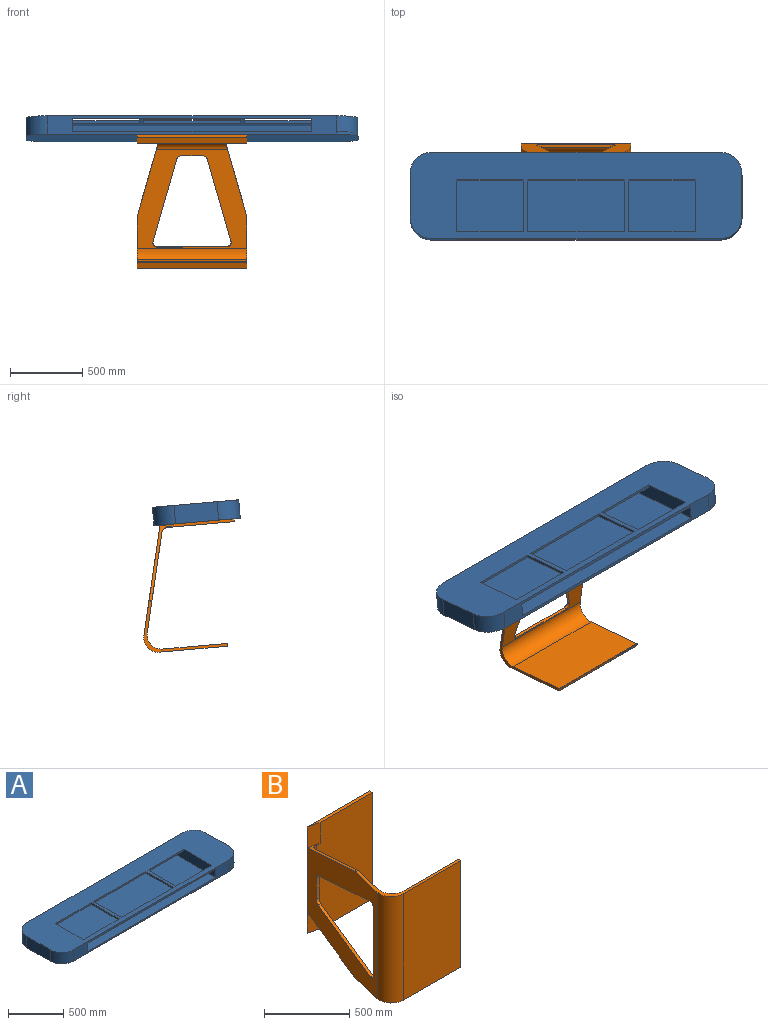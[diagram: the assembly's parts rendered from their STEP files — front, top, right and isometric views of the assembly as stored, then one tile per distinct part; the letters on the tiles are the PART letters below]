
ASSEMBLY  parts=2 mates=1
PART A: 28 faces, bbox 2300x600x128 mm
  f0: plane 1652x582mm, normal (0,0,1), area 961464mm2, adj f1,f6,f19,f27
  f1: plane 582x110mm, normal (-1,0,0), area 59988mm2, adj f0,f6,f13,f18,f21,f22,f27
  f2: plane 2000x128mm, normal (0,1,0), area 256000mm2, adj f3,f20,f21,f23,f26
  f3: cylinder r=150mm len=150mm, axis (0,0,-1), area 30159.3mm2, adj f2,f4,f21,f26
  f4: plane 300x128mm, normal (-1,0,0), area 38400mm2, adj f3,f5,f21,f26
  f5: cylinder r=150mm len=150mm, axis (0,0,-1), area 30159.3mm2, adj f4,f6,f21,f26
  f6: plane 2000x128mm, normal (0,-1,0), area 104016mm2, adj f0,f1,f5,f7,f19,f21,f22,f25
  f7: cylinder r=150mm len=150mm, axis (0,0,-1), area 25918.1mm2, adj f6,f8,f21,f25
  f8: plane 300x110mm, normal (1,0,0), area 33000mm2, adj f7,f20,f21,f24
  f9: plane 357x18mm, normal (-1,0,0), area 6426mm2, adj f10,f17,f21,f22
  f10: plane 668x18mm, normal (0,1,0), area 12024mm2, adj f9,f11,f21,f22
  f11: plane 357x18mm, normal (1,0,0), area 6426mm2, adj f10,f17,f21,f22
  f12: plane 358x18mm, normal (1,0,0), area 6444mm2, adj f13,f18,f21,f22
  f13: plane 462x18mm, normal (0,-1,0), area 8316mm2, adj f1,f12,f21,f22
  f14: plane 462x18mm, normal (0,-1,0), area 8316mm2, adj f15,f19,f21,f22
  f15: plane 358x18mm, normal (-1,0,0), area 6444mm2, adj f14,f16,f21,f22
  f16: plane 462x18mm, normal (0,1,0), area 8316mm2, adj f15,f19,f21,f22
  f17: plane 668x18mm, normal (0,-1,0), area 12024mm2, adj f9,f11,f21,f22
  f18: plane 462x18mm, normal (0,1,0), area 8316mm2, adj f1,f12,f21,f22
  f19: plane 582x110mm, normal (1,0,0), area 59988mm2, adj f0,f6,f14,f16,f21,f22,f27
  f20: cylinder r=150mm len=150mm, axis (0,0,-1), area 25918.1mm2, adj f2,f8,f21,f23
  f21: plane 2300x600mm, normal (0,0,1), area 791417.8mm2, adj f1,f2,f3,f4,f5,f6,f7,f8
  f22: plane 1652x582mm, normal (0,0,-1), area 392196mm2, adj f1,f6,f9,f10,f11,f12,f13,f14
  f23: cylinder r=150mm len=150mm, axis (0,0,1), area 4241.2mm2, adj f2,f20,f24,f26
  f24: plane 300x18mm, normal (1,0,0), area 5400mm2, adj f8,f23,f25,f26
  f25: cylinder r=150mm len=150mm, axis (0,0,1), area 4241.2mm2, adj f6,f7,f24,f26
  f26: plane 2300x600mm, normal (0,0,-1), area 1360685.8mm2, adj f2,f3,f4,f5,f6,f23,f24,f25
  f27: plane 1652x92mm, normal (0,-1,0), area 151984mm2, adj f0,f1,f19,f22
PART B: 31 faces, bbox 696.7x875.8x762 mm
  f0: plane 762x674.83mm, normal (0.97,-0.23,0), area 222758.4mm2, adj f2,f3,f10,f11,f17,f18,f19,f20
  f1: plane 762x752.78mm, normal (-0.97,0.23,0), area 268039.9mm2, adj f2,f3,f4,f14,f17,f18,f19,f20
  f2: plane 577.65x357.08mm, normal (0,0,1), area 18567mm2, adj f0,f1,f4,f5,f6,f7,f8,f9
  f3: plane 577.65x357.07mm, normal (0,0,-1), area 18566.9mm2, adj f0,f1,f4,f5,f6,f7,f8,f9
  f4: cylinder r=100mm len=762mm, axis (0,0,-1), area 137402.9mm2, adj f1,f2,f3,f5
  f5: plane 762x471.99mm, normal (0,-1,0), area 359655.6mm2, adj f2,f3,f4,f6
  f6: cylinder r=2mm len=762mm, axis (0,0,-1), area 2039.7mm2, adj f2,f3,f5,f7
  f7: plane 762x15.46mm, normal (0.97,-0.23,0), area 12107.8mm2, adj f2,f3,f6,f8
  f8: cylinder r=2mm len=762mm, axis (0,0,-1), area 2748.1mm2, adj f2,f3,f7,f9
  f9: plane 762x450.49mm, normal (0,1,0), area 343273.3mm2, adj f2,f3,f8,f10
  f10: cylinder r=100mm len=762mm, axis (0,0,-1), area 137402.9mm2, adj f0,f2,f3,f9
  f11: cylinder r=50mm len=493.16mm, axis (0,0,-1), area 31910.2mm2, adj f0,f12,f21,f24
  f12: plane 762x460.45mm, normal (0,-1,0), area 342170.1mm2, adj f11,f13,f15,f16,f21,f22,f23,f24
  f13: plane 762x20mm, normal (1,0,0), area 15240mm2, adj f12,f14,f15,f16
  f14: plane 762x515.82mm, normal (0,1,0), area 393054.2mm2, adj f1,f13,f15,f16,f22,f23
  f15: plane 515.82x20mm, normal (0,0,1), area 9471.3mm2, adj f12,f13,f14,f23
  f16: plane 515.82x20mm, normal (0,0,-1), area 9471.3mm2, adj f12,f13,f14,f22
  f17: plane 154.66x19.46mm, normal (-0.23,-0.97,0), area 3093.2mm2, adj f0,f1,f25,f28
  f18: plane 566.21x163.98mm, normal (-0.06,-0.27,0.96), area 11999.2mm2, adj f0,f1,f27,f28
  f19: plane 482.6x19.69mm, normal (0.23,0.97,0), area 9652mm2, adj f0,f1,f26,f27
  f20: plane 567.17x163.96mm, normal (-0.06,-0.27,-0.96), area 12018.1mm2, adj f0,f1,f25,f26
  f21: plane 515.36x205.39mm, normal (0.06,0.27,-0.96), area 11778.8mm2, adj f0,f1,f11,f12,f22,f30
  f22: plane 150.27x84.51mm, normal (-0.23,-0.97,0), area 13049.7mm2, adj f12,f14,f16,f21
  f23: plane 150x84.51mm, normal (-0.23,-0.97,0), area 13026.2mm2, adj f12,f14,f15,f24
  f24: plane 515.37x205.39mm, normal (0.06,0.27,0.96), area 11777.4mm2, adj f0,f1,f11,f12,f23,f29
  f25: cylinder r=30mm len=28.86mm, axis (0.97,-0.23,0), area 776.7mm2, adj f0,f1,f17,f20
  f26: cylinder r=30mm len=41.77mm, axis (0.97,-0.23,0), area 1109.5mm2, adj f0,f1,f19,f20
  f27: cylinder r=30mm len=41.78mm, axis (-0.97,0.23,0), area 1107.3mm2, adj f0,f1,f18,f19
  f28: cylinder r=30mm len=28.86mm, axis (-0.97,0.23,0), area 776.4mm2, adj f0,f1,f17,f18
  f29: cylinder r=30mm len=21.35mm, axis (0.97,-0.23,0), area 165.8mm2, adj f0,f1,f2,f24
  f30: cylinder r=30mm len=21.35mm, axis (-0.97,0.23,0), area 166.1mm2, adj f0,f1,f3,f21
PLACE A rot(axis=(-1,0,0),5deg) t=(0,-14.71,-2.18)mm
PLACE B rot(axis=(0.56,-0.61,-0.56),117.2deg) t=(381,228.3,-183.73)mm
MATE fastened B.f14 <-> A.f26  axis (0,0.09,1) through (0,-24.29,-111.76)mm
